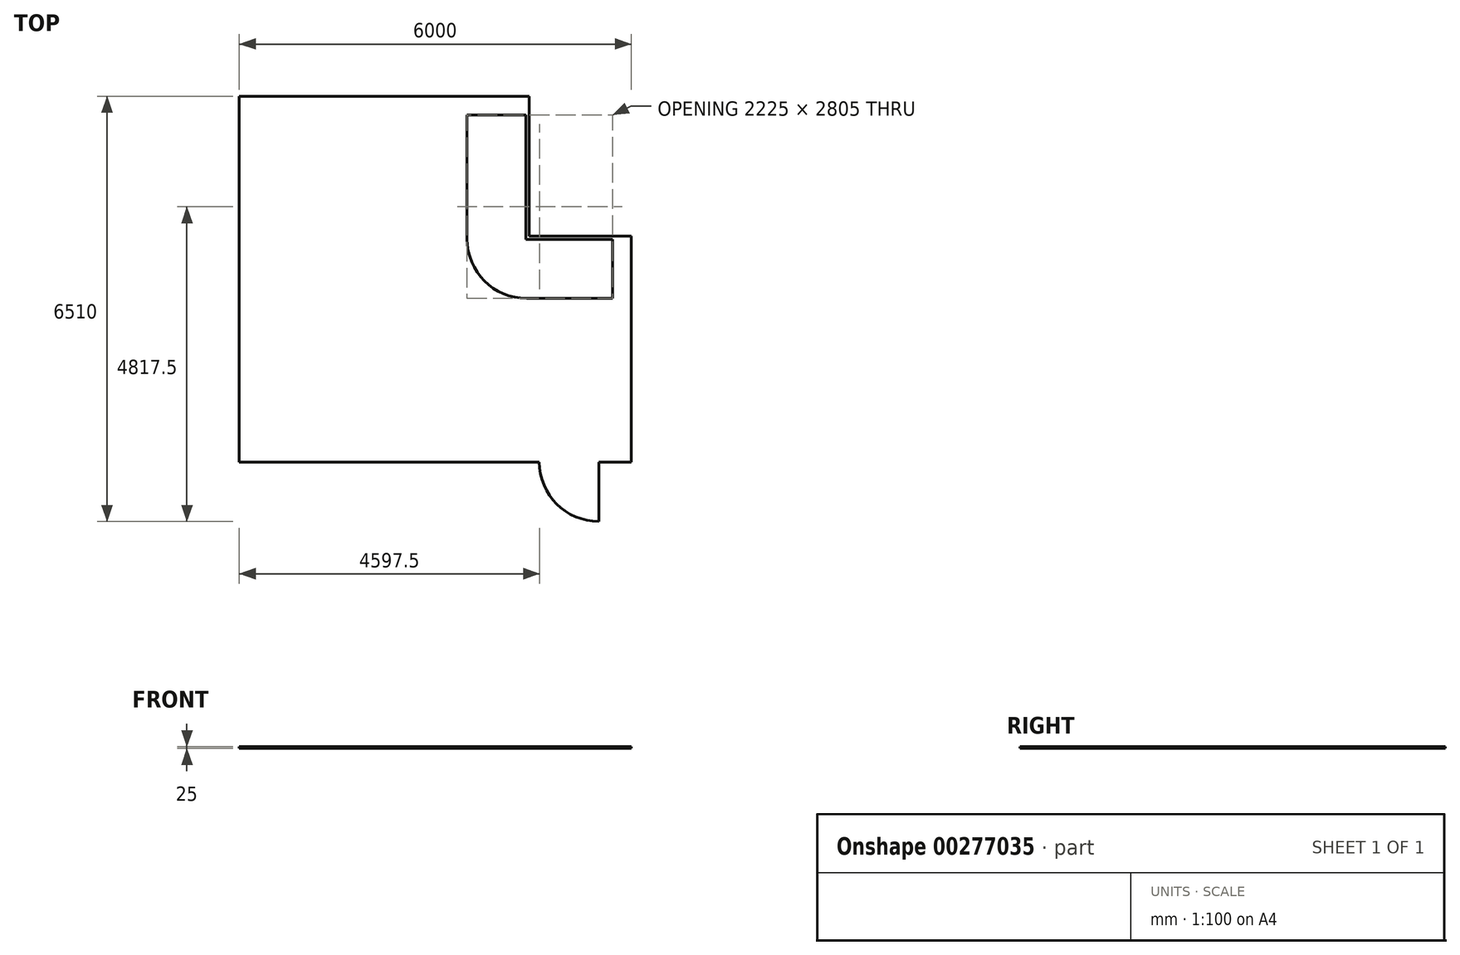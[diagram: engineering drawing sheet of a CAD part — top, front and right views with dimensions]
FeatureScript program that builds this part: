
annotation { "Feature Type Name" : "Feature", "Feature Type Description" : "" }
export const myFeature = defineFeature(function(context is Context, id is Id, definition is map)
    precondition{}
    {
        {
            var Q0;
            Q0=qCreatedBy(makeId("Top.planeOp"),FACE);
            var sketch = newSketch(context, id + "F0", { "sketchPlane" : qUnion([Q0])});
            skLineSegment(sketch, "E0", {"start": v(-2987.9, 1858.07) * mm, "end": v(-2987.9, -3741.93) * mm});
            skLineSegment(sketch, "E1", {"start": v(-2987.9, -3741.93) * mm, "end": v(1602.1, -3741.93) * mm});
            skLineSegment(sketch, "E2", {"start": v(3012.1, -3741.93) * mm, "end": v(3012.1, -1236.93) * mm});
            skLineSegment(sketch, "E3", {"start": v(3012.1, -1236.93) * mm, "end": v(1407.1, -1236.93) * mm});
            skLineSegment(sketch, "E4", {"start": v(497.1, -326.93) * mm, "end": v(497.1, 1858.07) * mm});
            skLineSegment(sketch, "E5", {"start": v(-2987.9, 1858.07) * mm, "end": v(497.1, 1858.07) * mm});
            skLineSegment(sketch, "E6", {"start": v(497.1, 1858.07) * mm, "end": v(1397.1, 1858.07) * mm});
            skLineSegment(sketch, "E7", {"start": v(3012.1, -1236.93) * mm, "end": v(3012.1, -336.93) * mm});
            skLineSegment(sketch, "E8", {"start": v(1397.1, 1858.07) * mm, "end": v(1397.1, -336.93) * mm});
            skLineSegment(sketch, "E9", {"start": v(1397.1, -336.93) * mm, "end": v(3012.1, -336.93) * mm});
            skLineSegment(sketch, "E10", {"start": v(1397.1, 1858.07) * mm, "end": v(1447.1, 1858.07) * mm});
            skLineSegment(sketch, "E11", {"start": v(1447.1, 1858.07) * mm, "end": v(1447.1, -286.93) * mm});
            skLineSegment(sketch, "E12", {"start": v(3012.1, -336.93) * mm, "end": v(3012.1, -286.93) * mm});
            skLineSegment(sketch, "E13", {"start": v(1447.1, -286.93) * mm, "end": v(3012.1, -286.93) * mm});
            skLineSegment(sketch, "E14", {"start": v(497.1, 1893.07) * mm, "end": v(497.1, 1858.07) * mm});
            skLineSegment(sketch, "E15", {"start": v(497.1, 1893.07) * mm, "end": v(497.1, 1568.07) * mm});
            skLineSegment(sketch, "E16", {"start": v(497.1, 1568.07) * mm, "end": v(497.1, 1278.07) * mm});
            skLineSegment(sketch, "E17", {"start": v(497.1, 1278.07) * mm, "end": v(497.1, 988.07) * mm});
            skLineSegment(sketch, "E18", {"start": v(497.1, 1568.07) * mm, "end": v(1397.1, 1568.07) * mm});
            skLineSegment(sketch, "E19", {"start": v(497.1, 1278.07) * mm, "end": v(1397.1, 1278.07) * mm});
            skLineSegment(sketch, "E20", {"start": v(497.1, 1858.07) * mm, "end": v(947.1, 1858.07) * mm});
            skLineSegment(sketch, "E21", {"start": v(3012.1, -1236.93) * mm, "end": v(2722.1, -1236.93) * mm});
            skLineSegment(sketch, "E22", {"start": v(2722.1, -1236.93) * mm, "end": v(2432.1, -1236.93) * mm});
            skLineSegment(sketch, "E23", {"start": v(2432.1, -1236.93) * mm, "end": v(2142.1, -1236.93) * mm});
            skLineSegment(sketch, "E24", {"start": v(2142.1, -1236.93) * mm, "end": v(1852.1, -1236.93) * mm});
            skLineSegment(sketch, "E25", {"start": v(2722.1, -1236.93) * mm, "end": v(2722.1, -336.93) * mm});
            skLineSegment(sketch, "E26", {"start": v(2432.1, -1236.93) * mm, "end": v(2432.1, -336.93) * mm});
            skLineSegment(sketch, "E27", {"start": v(2142.1, -1236.93) * mm, "end": v(2142.1, -336.93) * mm});
            skLineSegment(sketch, "E28", {"start": v(1852.1, -1236.93) * mm, "end": v(1852.1, -336.93) * mm});
            skPoint(sketch, "E29.visualSharp", {"position": v(497.1, -1236.93) * mm});
            skArc(sketch, "E29.filletArc", {"start": v(497.1, -326.93) * mm, "mid": v(763.64, -970.4) * mm, "end": v(1407.1, -1236.93) * mm});
            skPoint(sketch, "E30.visualSharp", {"position": v(947.1, 168.07) * mm});
            skLineSegment(sketch, "E31", {"start": v(497.1, 988.07) * mm, "end": v(1397.1, 988.07) * mm});
            skLineSegment(sketch, "E32", {"start": v(497.1, 988.07) * mm, "end": v(497.1, 698.07) * mm});
            skLineSegment(sketch, "E33", {"start": v(497.1, 698.07) * mm, "end": v(497.1, 408.07) * mm});
            skLineSegment(sketch, "E34", {"start": v(497.1, 408.07) * mm, "end": v(497.1, 118.07) * mm});
            skLineSegment(sketch, "E35", {"start": v(497.1, 698.07) * mm, "end": v(1397.1, 698.07) * mm});
            skLineSegment(sketch, "E36", {"start": v(497.1, 408.07) * mm, "end": v(1397.1, 408.07) * mm});
            skLineSegment(sketch, "E37", {"start": v(497.1, 118.07) * mm, "end": v(1397.1, 118.07) * mm});
            skLineSegment(sketch, "E38", {"start": v(947.1, 1858.07) * mm, "end": v(947.1, 118.07) * mm});
            skLineSegment(sketch, "E39", {"start": v(3012.1, -336.93) * mm, "end": v(3012.1, -786.93) * mm});
            skLineSegment(sketch, "E40", {"start": v(947.1, 1858.07) * mm, "end": v(947.1, -281.93) * mm});
            skPoint(sketch, "E41.orphan", {"position": v(1852.1, -786.93) * mm});
            skLineSegment(sketch, "E42", {"start": v(1402.1, -736.93) * mm, "end": v(3012.1, -736.93) * mm});
            skPoint(sketch, "E43.visualSharp", {"position": v(947.1, -736.93) * mm});
            skArc(sketch, "E43.filletArc", {"start": v(947.1, -281.93) * mm, "mid": v(1080.38, -603.67) * mm, "end": v(1402.1, -736.93) * mm});
            skLineSegment(sketch, "E44", {"start": v(3012.1, -3741.93) * mm, "end": v(2512.1, -3741.93) * mm});
            skPoint(sketch, "E45.end.orphan", {"position": v(1602.1, -3741.93) * mm});
            skLineSegment(sketch, "E46.trimOffspring", {"start": v(2512.1, -3741.93) * mm, "end": v(3012.1, -3741.93) * mm});
            skArc(sketch, "E47", {"start": v(1602.1, -3741.93) * mm, "mid": v(1868.64, -4385.4) * mm, "end": v(2512.1, -4651.93) * mm});
            skLineSegment(sketch, "E48", {"start": v(2512.1, -3741.93) * mm, "end": v(2512.1, -4651.93) * mm});
            skSolve(sketch);
        }
        {
            var Q0;
            Q0 = qSketchRegion(id + "F0", true);
            extrude(context, id + "F1", {"entities" : qUnion([Q0]), "depth" : 25 * mm});
        }
    });
